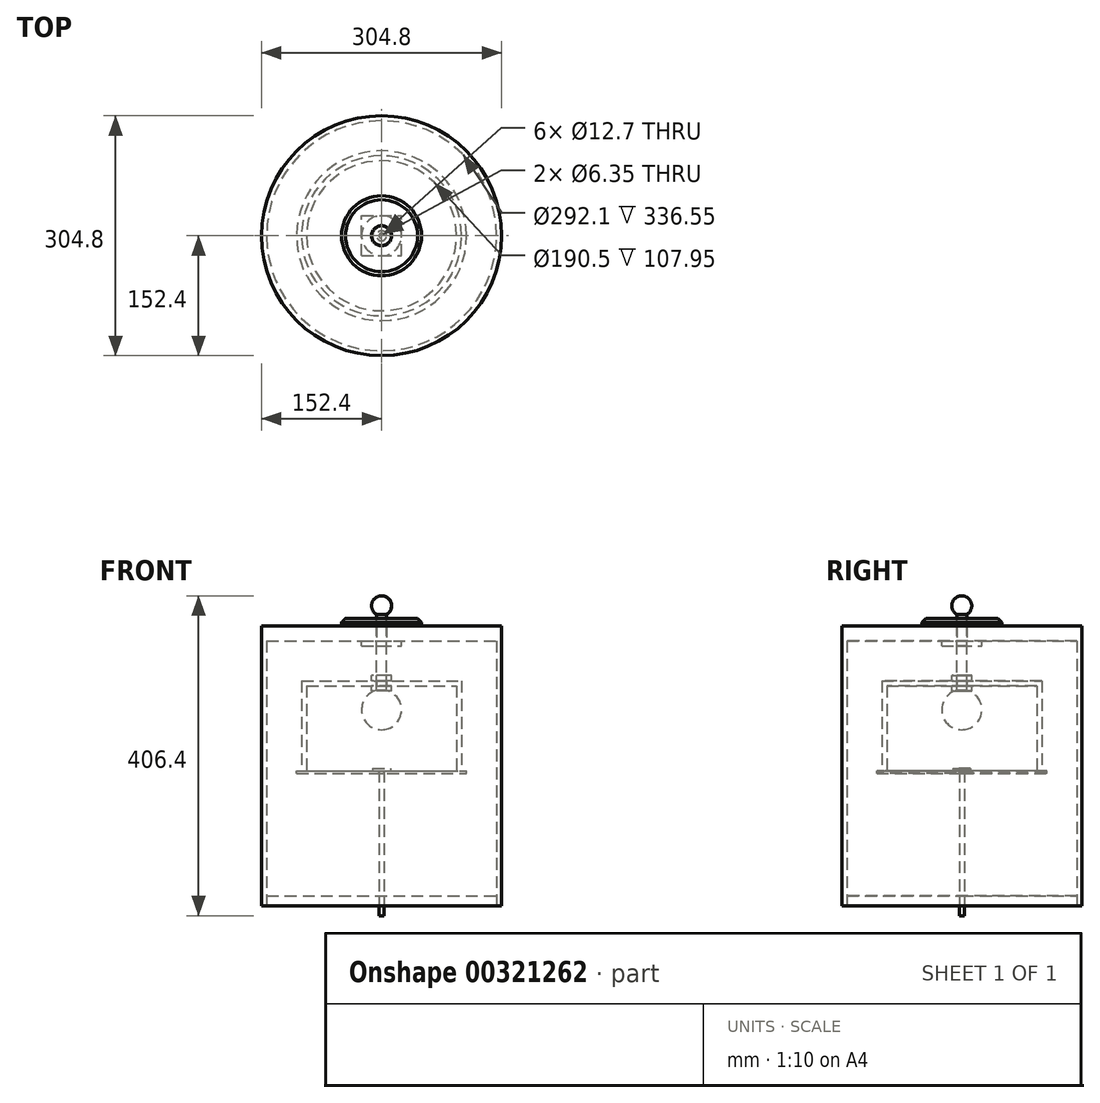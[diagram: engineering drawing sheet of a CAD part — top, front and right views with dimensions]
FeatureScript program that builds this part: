
annotation { "Feature Type Name" : "Feature", "Feature Type Description" : "" }
export const myFeature = defineFeature(function(context is Context, id is Id, definition is map)
    precondition{}
    {
        {
            var Q0;
            Q0=qCreatedBy(makeId("Front.planeOp"),FACE);
            var sketch = newSketch(context, id + "F0", { "sketchPlane" : qUnion([Q0])});
            skLineSegment(sketch, "E0", {"start": v(6.35, 0) * mm, "end": v(152.4, 0) * mm});
            skLineSegment(sketch, "E1", {"start": v(152.4, 0) * mm, "end": v(152.4, -355.6) * mm});
            skLineSegment(sketch, "E2", {"start": v(152.4, -355.6) * mm, "end": v(146.05, -355.6) * mm});
            skLineSegment(sketch, "E3", {"start": v(0, -400.05) * mm, "end": v(0, -355.6) * mm});
            skLineSegment(sketch, "E4", {"start": v(146.05, -349.25) * mm, "end": v(146.05, -19.05) * mm});
            skLineSegment(sketch, "E5", {"start": v(146.05, -19.05) * mm, "end": v(6.35, -19.05) * mm});
            skLineSegment(sketch, "E6", {"start": v(6.35, 0) * mm, "end": v(6.35, -19.05) * mm});
            skPoint(sketch, "E7.orphan", {"position": v(0, -19.05) * mm});
            skLineSegment(sketch, "E8", {"start": v(146.05, -349.25) * mm, "end": v(146.05, -355.6) * mm});
            skSolve(sketch);
        }
        {
            var Q0;
            Q0=makeQuery(id+"F0.imprint","IMPRINT",FACE,{"disambiguationData":[TD([[makeQuery(id+"F0.imprint","IMPRINT",EDGE,{"derivedFrom":sQuery(id+"F0.wireOp",EDGE,"E0")}),-1.0]])]});
            var Q1;
            Q1=sQuery(id+"F0.wireOp",EDGE,"E3");
            revolve(context, id + "F1", {"entities" : qUnion([Q0]), "axis" : qUnion([Q1]), "revolveType" : RevolveType.FULL});
        }
        {
            var Q0;
            Q0=qCreatedBy(makeId("Front.planeOp"),FACE);
            var sketch = newSketch(context, id + "F2", { "sketchPlane" : qUnion([Q0])});
            skLineSegment(sketch, "E9", {"start": v(0, 0) * mm, "end": v(50.8, 0) * mm});
            skLineSegment(sketch, "E10", {"start": v(50.8, 0) * mm, "end": v(50.8, 9.53) * mm});
            skLineSegment(sketch, "E11", {"start": v(50.8, 9.53) * mm, "end": v(6.35, 9.52) * mm});
            skLineSegment(sketch, "E12", {"start": v(0, 12.7) * mm, "end": v(0, 0) * mm});
            skLineSegment(sketch, "E13", {"start": v(6.35, 9.52) * mm, "end": v(6.35, 0) * mm});
            skSolve(sketch);
        }
        {
            var Q0;
            Q0=makeQuery(id+"F2.imprint","IMPRINT",FACE,{"disambiguationData":[TD([[makeQuery(id+"F2.imprint","IMPRINT",EDGE,{"derivedFrom":sQuery(id+"F2.wireOp",EDGE,"E9")}),1.0]])]});
            var Q1;
            Q1=sQuery(id+"F2.wireOp",EDGE,"E12");
            revolve(context, id + "F3", {"entities" : qUnion([Q0]), "axis" : qUnion([Q1]), "revolveType" : RevolveType.FULL});
        }
        {
            var Q0;
            Q0=qCreatedBy(makeId("Front.planeOp"),FACE);
            var sketch = newSketch(context, id + "F4", { "sketchPlane" : qUnion([Q0])});
            skLineSegment(sketch, "E14", {"start": v(0, 0) * mm, "end": v(0, -81.28) * mm});
            skLineSegment(sketch, "E15", {"start": v(6.35, -82.09) * mm, "end": v(6.35, 0) * mm});
            skLineSegment(sketch, "E16", {"start": v(6.35, 0) * mm, "end": v(0, 0) * mm});
            skLineSegment(sketch, "E17", {"start": v(6.35, 0) * mm, "end": v(6.35, 14.4) * mm});
            skArc(sketch, "E18", {"start": v(6.35, 14.4) * mm, "mid": v(12.27, 28.69) * mm, "end": v(0, 38.1) * mm});
            skLineSegment(sketch, "E19", {"start": v(0, 0) * mm, "end": v(0, 38.1) * mm});
            skArc(sketch, "E20", {"start": v(0, -132.08) * mm, "mid": v(25.2, -109.88) * mm, "end": v(6.35, -82.09) * mm});
            skPoint(sketch, "E21.orphan", {"position": v(0, -82.55) * mm});
            skLineSegment(sketch, "E22", {"start": v(0, -81.28) * mm, "end": v(0, -132.08) * mm});
            skSolve(sketch);
        }
        {
            var Q0;
            Q0=qSketchRegion(id+"F4",true);
            var Q1;
            Q1=sQuery(id+"F4.wireOp",EDGE,"E14");
            revolve(context, id + "F5", {"entities" : qUnion([Q0]), "axis" : qUnion([Q1]), "revolveType" : RevolveType.FULL});
        }
        {
            var Q0;
            Q0=qCreatedBy(makeId("Front.planeOp"),FACE);
            var sketch = newSketch(context, id + "F6", { "sketchPlane" : qUnion([Q0])});
            skLineSegment(sketch, "E23", {"start": v(6.35, -69.85) * mm, "end": v(101.6, -69.85) * mm});
            skLineSegment(sketch, "E24", {"start": v(101.6, -69.85) * mm, "end": v(101.6, -184.15) * mm});
            skLineSegment(sketch, "E25", {"start": v(101.6, -184.15) * mm, "end": v(95.25, -184.15) * mm});
            skLineSegment(sketch, "E26", {"start": v(0, -335.92) * mm, "end": v(0, -184.15) * mm});
            skLineSegment(sketch, "E27", {"start": v(95.25, -228.6) * mm, "end": v(95.25, -76.2) * mm});
            skLineSegment(sketch, "E28", {"start": v(95.25, -76.2) * mm, "end": v(6.35, -76.2) * mm});
            skLineSegment(sketch, "E29", {"start": v(0, -76.2) * mm, "end": v(0, -69.85) * mm});
            skLineSegment(sketch, "E30", {"start": v(95.25, -184.15) * mm, "end": v(95.25, -228.6) * mm});
            skLineSegment(sketch, "E31", {"start": v(6.35, -69.85) * mm, "end": v(6.35, -76.2) * mm});
            skSolve(sketch);
        }
        {
            var Q0;
            Q0=qSketchRegion(id+"F6",true);
            var Q1;
            Q1=sQuery(id+"F6.wireOp",EDGE,"E29");
            revolve(context, id + "F7", {"entities" : qUnion([Q0]), "axis" : qUnion([Q1]), "revolveType" : RevolveType.FULL});
        }
        {
            var Q0;
            Q0=qCreatedBy(makeId("Front.planeOp"),FACE);
            var sketch = newSketch(context, id + "F8", { "sketchPlane" : qUnion([Q0])});
            skLineSegment(sketch, "E32.bottom", {"start": v(6.35, -69.85) * mm, "end": v(12.7, -69.85) * mm});
            skLineSegment(sketch, "E32.top", {"start": v(6.35, -63.09) * mm, "end": v(12.7, -63.09) * mm});
            skLineSegment(sketch, "E32.left", {"start": v(6.35, -69.85) * mm, "end": v(6.35, -63.09) * mm});
            skLineSegment(sketch, "E32.right", {"start": v(12.7, -69.85) * mm, "end": v(12.7, -63.09) * mm});
            skLineSegment(sketch, "E33.bottom", {"start": v(6.35, -76.2) * mm, "end": v(12.7, -76.2) * mm});
            skLineSegment(sketch, "E33.top", {"start": v(6.35, -82.96) * mm, "end": v(12.7, -82.96) * mm});
            skLineSegment(sketch, "E33.left", {"start": v(6.35, -76.2) * mm, "end": v(6.35, -82.96) * mm});
            skLineSegment(sketch, "E33.right", {"start": v(12.7, -76.2) * mm, "end": v(12.7, -82.96) * mm});
            skLineSegment(sketch, "E34", {"start": v(0, -57.88) * mm, "end": v(0, -89.68) * mm, "construction": true});
            skSolve(sketch);
        }
        {
            var Q0;
            Q0=makeQuery(id+"F8.imprint","IMPRINT",FACE,{"disambiguationData":[TD([[makeQuery(id+"F8.imprint","IMPRINT",EDGE,{"derivedFrom":sQuery(id+"F8.wireOp",EDGE,"E32.bottom")}),1.0]])]});
            var Q1;
            Q1=makeQuery(id+"F8.imprint","IMPRINT",FACE,{"disambiguationData":[TD([[makeQuery(id+"F8.imprint","IMPRINT",EDGE,{"derivedFrom":sQuery(id+"F8.wireOp",EDGE,"E33.bottom")}),-1.0]])]});
            var Q2;
            Q2=sQuery(id+"F8.wireOp",EDGE,"E34");
            revolve(context, id + "F9", {"entities" : qUnion([Q0, Q1]), "axis" : qUnion([Q2]), "revolveType" : RevolveType.FULL});
        }
        {
            var Q0;
            Q0=makeQuery(id+"F7.opRevolve","SWEPT_FACE",FACE,{"disambiguationData":[OSD([sQuery(id+"F6.wireOp",EDGE,"E25")])]});
            var sketch = newSketch(context, id + "F10", { "sketchPlane" : qUnion([Q0])});
            skCircle(sketch, "E35", {"center": v(0, 0) * mm, "radius": 107.95 * mm});
            skCircle(sketch, "E36", {"center": v(0, 0) * mm, "radius": 3.18 * mm});
            skSolve(sketch);
        }
        {
            var Q0;
            Q0=makeQuery(id+"F10.imprint","IMPRINT",FACE,{"disambiguationData":[TD([[makeQuery(id+"F10.imprint","IMPRINT",EDGE,{"derivedFrom":sQuery(id+"F10.wireOp",EDGE,"E35")}),1.0]])]});
            var Q1;
            Q1=makeQuery(id+"F10.imprint","IMPRINT",FACE,{"disambiguationData":[TD([[makeQuery(id+"F10.imprint","IMPRINT",EDGE,{"derivedFrom":makeQuery(id+"F7.opRevolve","SWEPT_EDGE",EDGE,{"disambiguationData":[OSD([sQuery(id+"F6.wireOp",EDGE,"E25"),sQuery(id+"F6.wireOp",EDGE,"E27")])]})}),1.0]])]});
            var Q2;
            {var subQ0=sQuery(id+"F6.wireOp",EDGE,"E25");Q2=makeQuery(id+"F10.imprint","IMPRINT",FACE,{"disambiguationData":[TD([[makeQuery(id+"F10.imprint","IMPRINT",EDGE,{"derivedFrom":makeQuery(id+"F7.opRevolve","SWEPT_EDGE",EDGE,{"disambiguationData":[OSD([sQuery(id+"F6.wireOp",EDGE,"E24"),subQ0])]})}),1.0]])]});}
            extrude(context, id + "F11", {"entities" : qUnion([Q0, Q1, Q2]), "depth" : 3.17 * mm});
        }
        {
            var Q0;
            Q0=makeQuery(id+"F3.opRevolve","SWEPT_EDGE",EDGE,{"disambiguationData":[OSD([sQuery(id+"F2.wireOp",EDGE,"E10"),sQuery(id+"F2.wireOp",EDGE,"E11")])]});
            chamfer(context, id + "F12", {"entities" : qUnion([Q0]), "width" : 5.08 * mm, "tangentPropagation" : true});
        }
        {
            var Q0;
            Q0=qCreatedBy(makeId("Front.planeOp"),FACE);
            var sketch = newSketch(context, id + "F13", { "sketchPlane" : qUnion([Q0])});
            skLineSegment(sketch, "E37", {"start": v(0, -180.97) * mm, "end": v(11.22, -180.97) * mm});
            skLineSegment(sketch, "E38", {"start": v(11.22, -180.97) * mm, "end": v(11.22, -184.15) * mm});
            skLineSegment(sketch, "E39", {"start": v(11.22, -184.15) * mm, "end": v(3.17, -184.15) * mm});
            skLineSegment(sketch, "E40", {"start": v(3.17, -184.15) * mm, "end": v(3.18, -368.3) * mm});
            skLineSegment(sketch, "E41", {"start": v(3.18, -368.3) * mm, "end": v(0, -368.3) * mm});
            skLineSegment(sketch, "E42", {"start": v(0, -368.3) * mm, "end": v(0, -180.97) * mm});
            skSolve(sketch);
        }
        {
            var Q0;
            Q0=makeQuery(id+"F13.imprint","IMPRINT",FACE,{"disambiguationData":[TD([[makeQuery(id+"F13.imprint","IMPRINT",EDGE,{"derivedFrom":sQuery(id+"F13.wireOp",EDGE,"E37")}),-1.0]])]});
            var Q1;
            Q1=sQuery(id+"F13.wireOp",EDGE,"E42");
            revolve(context, id + "F14", {"entities" : qUnion([Q0]), "axis" : qUnion([Q1]), "revolveType" : RevolveType.FULL});
        }
        {
            var Q0;
            Q0=makeQuery(id+"F1.opRevolve","SWEPT_FACE",FACE,{"disambiguationData":[OSD([sQuery(id+"F0.wireOp",EDGE,"E5")])]});
            var sketch = newSketch(context, id + "F15", { "sketchPlane" : qUnion([Q0])});
            skLineSegment(sketch, "E43.bottom", {"start": v(-25.4, 25.4) * mm, "end": v(25.4, 25.4) * mm});
            skLineSegment(sketch, "E43.top", {"start": v(-25.4, -25.4) * mm, "end": v(25.4, -25.4) * mm});
            skLineSegment(sketch, "E43.left", {"start": v(-25.4, 25.4) * mm, "end": v(-25.4, -25.4) * mm});
            skLineSegment(sketch, "E43.right", {"start": v(25.4, 25.4) * mm, "end": v(25.4, -25.4) * mm});
            skPoint(sketch, "E43.middle", {"position": v(0, 0) * mm});
            skSolve(sketch);
        }
        {
            var Q0;
            Q0=makeQuery(id+"F15.imprint","IMPRINT",FACE,{"disambiguationData":[TD([[makeQuery(id+"F15.imprint","IMPRINT",EDGE,{"derivedFrom":sQuery(id+"F15.wireOp",EDGE,"E43.bottom")}),-1.0]])]});
            extrude(context, id + "F16", {"entities" : qUnion([Q0]), "depth" : 6.35 * mm});
        }
        {
            var Q0;
            Q0=makeQuery(id+"F1.opRevolve","SWEPT_FACE",FACE,{"disambiguationData":[OSD([sQuery(id+"F0.wireOp",EDGE,"E2")])]});
            var sketch = newSketch(context, id + "F17", { "sketchPlane" : qUnion([Q0])});
            skCircle(sketch, "E44", {"center": v(0, 0) * mm, "radius": 146.05 * mm});
            skCircle(sketch, "E45", {"center": v(0, 0) * mm, "radius": 3.18 * mm});
            skSolve(sketch);
        }
        {
            var Q0;
            Q0=makeQuery(id+"F17.imprint","IMPRINT",FACE,{"disambiguationData":[TD([[makeQuery(id+"F17.imprint","IMPRINT",EDGE,{"derivedFrom":sQuery(id+"F17.wireOp",EDGE,"E44")}),1.0]])]});
            extrude(context, id + "F18", {"entities" : qUnion([Q0]), "oppositeDirection" : true, "depth" : 12.7 * mm});
        }
    });
